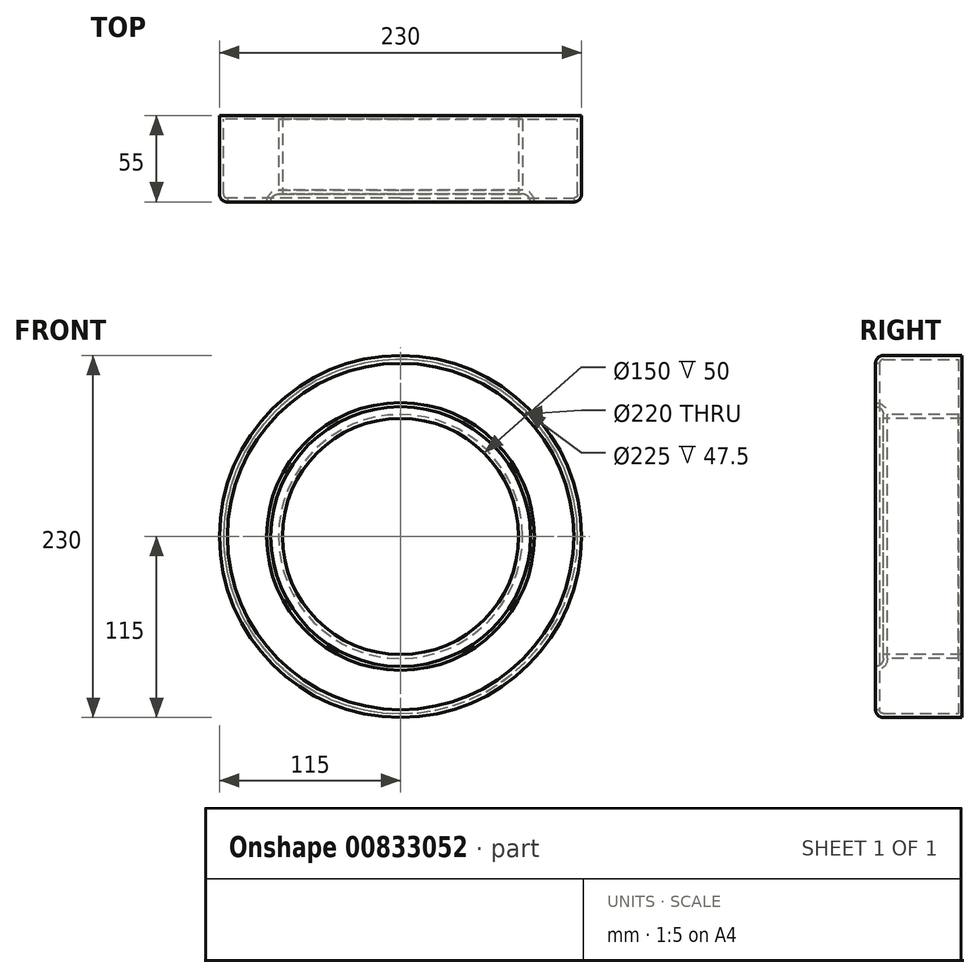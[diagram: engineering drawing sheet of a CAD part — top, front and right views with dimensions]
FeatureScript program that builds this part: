
annotation { "Feature Type Name" : "Feature", "Feature Type Description" : "" }
export const myFeature = defineFeature(function(context is Context, id is Id, definition is map)
    precondition{}
    {
        {
            var Q0;
            Q0=qCreatedBy(makeId("Front.planeOp"),FACE);
            var sketch = newSketch(context, id + "F0", { "sketchPlane" : qUnion([Q0])});
            skCircle(sketch, "E0", {"center": v(0, 0) * mm, "radius": 115 * mm});
            skSolve(sketch);
        }
        {
            var Q0;
            Q0 = qSketchRegion(id + "F0", true);
            extrude(context, id + "F1", {"entities" : qUnion([Q0]), "depth" : 55 * mm, "offsetDistance" : 25 * mm});
        }
        {
            var Q0;
            Q0=makeQuery(id+"F1.opExtrude","CAP_FACE",FACE,{"disambiguationData":[OSD([sQuery(id+"F0.wireOp",EDGE,"E0")])],"isStart":false});
            var sketch = newSketch(context, id + "F2", { "sketchPlane" : qUnion([Q0])});
            skCircle(sketch, "E1", {"center": v(0, 0) * mm, "radius": 82.5 * mm});
            skCircle(sketch, "E2", {"center": v(0, 0) * mm, "radius": 75 * mm});
            skSolve(sketch);
        }
        {
            var Q0;
            Q0=makeQuery(id+"F2.imprint","IMPRINT",FACE,{"disambiguationData":[TD([[makeQuery(id+"F2.imprint","IMPRINT",EDGE,{"derivedFrom":sQuery(id+"F2.wireOp",EDGE,"E1")}),1.0]])]});
            extrude(context, id + "F3", {"entities" : qUnion([Q0]), "operationType" : NewBodyOperationType.REMOVE, "oppositeDirection" : true, "depth" : 5 * mm, "offsetDistance" : 25 * mm});
        }
        {
            var Q0;
            Q0=makeQuery(id+"F3.boolean.opBoolean","SPLIT",FACE,{"disambiguationData":[TD([makeQuery(id+"F3.opExtrude","SWEPT_FACE",FACE,{"disambiguationData":[OSD([sQuery(id+"F2.wireOp",EDGE,"E2")])]})])],"derivedFrom":makeQuery(id+"F1.opExtrude","CAP_FACE",FACE,{"disambiguationData":[OSD([sQuery(id+"F0.wireOp",EDGE,"E0")])],"isStart":false})});
            extrude(context, id + "F4", {"entities" : qUnion([Q0]), "operationType" : NewBodyOperationType.REMOVE, "oppositeDirection" : true, "depth" : 55 * mm, "offsetDistance" : 25 * mm});
        }
        {
            var Q0;
            Q0=makeQuery(id+"F3.boolean.opBoolean","COPY",EDGE,{"derivedFrom":makeQuery(id+"F3.opExtrude","CAP_EDGE",EDGE,{"disambiguationData":[OSD([sQuery(id+"F2.wireOp",EDGE,"E1")])],"isStart":false})});
            fillet(context, id + "F5", {"entities" : qUnion([Q0]), "radius" : 5 * mm, "tangentPropagation" : true, "allowEdgeOverflow" : false});
        }
        {
            var Q0;
            Q0=makeQuery(id+"F1.opExtrude","CAP_EDGE",EDGE,{"disambiguationData":[OSD([sQuery(id+"F0.wireOp",EDGE,"E0")])],"isStart":false});
            fillet(context, id + "F6", {"entities" : qUnion([Q0]), "radius" : 5 * mm, "tangentPropagation" : true, "allowEdgeOverflow" : false});
        }
        {
            var Q0;
            {var subQ0=sQuery(id+"F0.wireOp",EDGE,"E0");Q0=makeQuery(id+"F3.boolean.opBoolean","SPLIT",FACE,{"disambiguationData":[TD([makeQuery(id+"F1.opExtrude","SWEPT_FACE",FACE,{"disambiguationData":[OSD([subQ0])]})])],"derivedFrom":makeQuery(id+"F1.opExtrude","CAP_FACE",FACE,{"disambiguationData":[OSD([subQ0])],"isStart":false})});}
            shell(context, id + "F7", {"entities" : qUnion([Q0]), "thickness" : 2.5 * mm});
        }
    });
